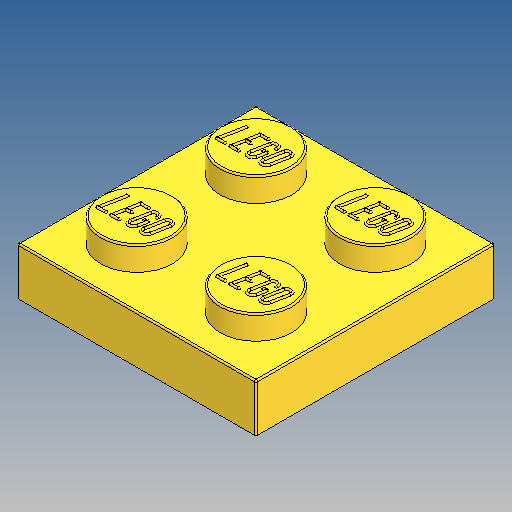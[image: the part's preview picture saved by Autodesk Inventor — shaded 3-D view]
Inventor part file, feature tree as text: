
AUTODESK INVENTOR PART (.ipt)
format: ipt  version: 2025 (Build 290162010, 162A)  size: 4,701,696 bytes
history: native  units: in
note: dims shown in document units (in); Inventor stores cm internally (conversion verified against a paired STEP export)
features: extrude x4, sketch x4, fillet x2, pattern_linear x2, other x1
ambient origin geometry x8: Origin, YZ Plane, XZ Plane, XY Plane, X Axis, Y Axis, Z Axis, Center Point
bodies: Solid1 (feature_tree)
feature tree (13):
  extrude  "Extrusion1"  Depth=0.6299in
  extrude  "Extrusion4"  Depth=0.063in
  other  "LEGO:1"
  fillet  "Fillet2"  Radius=0.063in
  pattern_linear  "Rectangular Pattern1"  Spacing1=0.189in  [1 undecoded]
  sketch  "Sketch3"  dims[d4=0.126in d5=0.0in d7=0.0591in d8=0.063in d11=0.063in d12=0.0in]
  extrude  "Extrusion2"  Depth=0.063in
  extrude  "Extrusion5"  Depth=0.189in
  pattern_linear  "Rectangular Pattern2"  Spacing1=0.1575in  [1 undecoded]
  fillet  "Fillet1"  Radius=0.1575in
  sketch  "Sketch2"  dims[d0=0.6299in d1=0.6299in]
  sketch  "Sketch9"  dims[d22=0.0039in]
  sketch  "Sketch10"  dims[d60=0.2564in d61=0.189in d62=0.063in d63=0.189in d64=0.1575in d65=0.1575in d66=0.063in d67=0.0in d68=0.0039in d69=0.7874in d71=0.315in d72=0.7874in d74=0.315in d75=0.315in d76=0.315in d77=0.0709in d78=0.0in d79=0.3937in d81=0.315in d82=0.3937in d84=0.315in d85=0.0in d86=0.0in d87=0.0in d88=0.0in d89=0.0in d90=0.0in d91=0.0in d92=0.0079in d93=0.0732in d94=0.0281in d95=0.035in d96=0.0079in d97=0.0139in d98=0.0281in d99=0.035in d100=0.0281in d101=0.0159in d102=0.0177in d103=0.035in d104=0.5428in]
note: 2 required parameter values undecoded (feature->parameter linkage not recoverable at this tier; creation-order binding heuristic only, values carry confidence <= 0.55)
